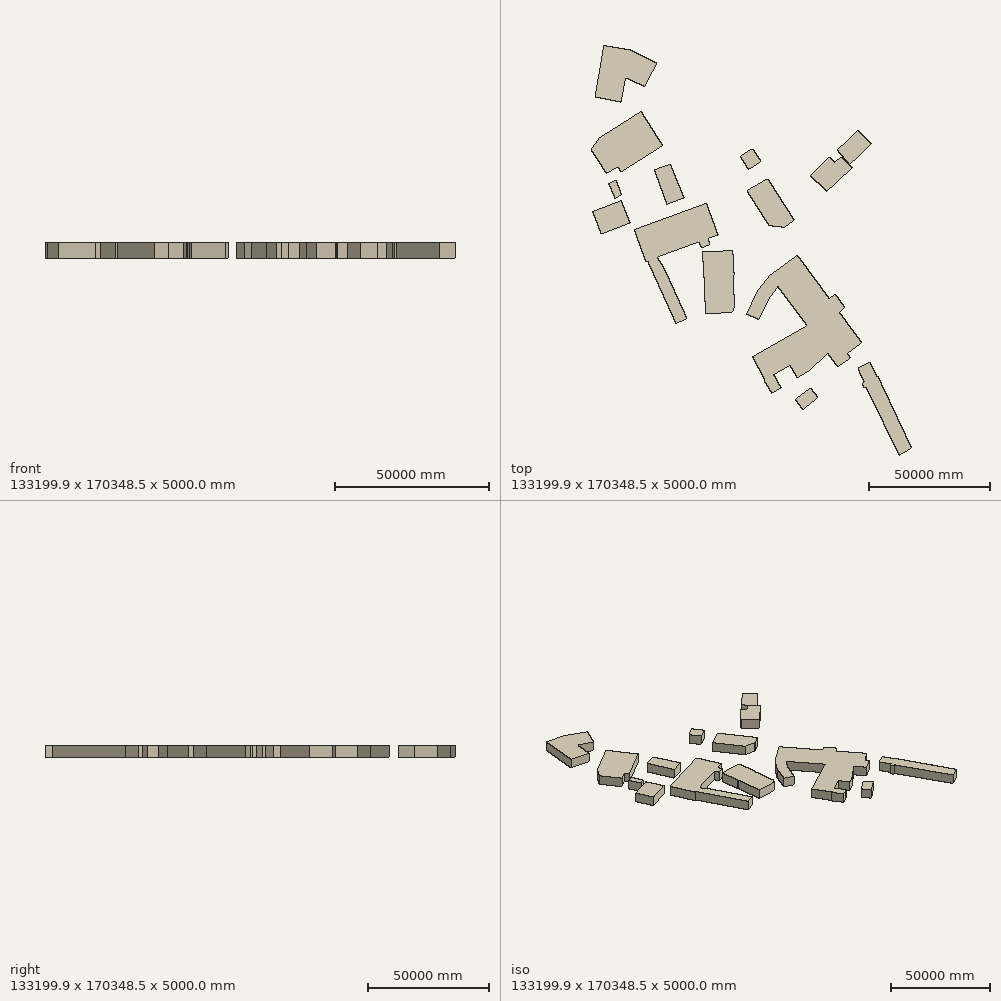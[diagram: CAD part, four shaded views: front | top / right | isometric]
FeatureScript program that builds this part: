
annotation { "Feature Type Name" : "Feature", "Feature Type Description" : "" }
export const myFeature = defineFeature(function(context is Context, id is Id, definition is map)
    precondition{}
    {
        {
            var Q0;
            Q0=qCreatedBy(makeId("Top.planeOp"),FACE);
            var sketch = newSketch(context, id + "F0", { "sketchPlane" : qUnion([Q0])});
            skLineSegment(sketch, "E0", {"start": v(9180.3, 14744.96) * mm, "end": v(-20829.56, 3751.13) * mm});
            skLineSegment(sketch, "E1", {"start": v(-20829.56, 3751.13) * mm, "end": v(-16013.77, -9394.52) * mm});
            skLineSegment(sketch, "E2", {"start": v(-16013.77, -9394.52) * mm, "end": v(13996.08, 1599.31) * mm});
            skLineSegment(sketch, "E3", {"start": v(13996.08, 1599.31) * mm, "end": v(9180.3, 14744.96) * mm});
            skLineSegment(sketch, "E4", {"start": v(-5833.22, 31019.04) * mm, "end": v(-12464.48, 28589.74) * mm});
            skLineSegment(sketch, "E5", {"start": v(-12464.48, 28589.74) * mm, "end": v(-7236.84, 14319.86) * mm});
            skLineSegment(sketch, "E6", {"start": v(-7236.84, 14319.86) * mm, "end": v(-97.14, 16935.42) * mm});
            skLineSegment(sketch, "E7", {"start": v(-97.14, 16935.42) * mm, "end": v(-5833.22, 31019.04) * mm});
            skLineSegment(sketch, "E8", {"start": v(7534.29, -5269.84) * mm, "end": v(20121.82, -4941.47) * mm});
            skLineSegment(sketch, "E9", {"start": v(20121.82, -4941.47) * mm, "end": v(20705.59, -15376.35) * mm});
            skLineSegment(sketch, "E10", {"start": v(20705.59, -15376.35) * mm, "end": v(8060.17, -16083.79) * mm});
            skLineSegment(sketch, "E11", {"start": v(8060.17, -16083.79) * mm, "end": v(7534.29, -5269.84) * mm});
            skLineSegment(sketch, "E12", {"start": v(20339.95, -15396.8) * mm, "end": v(20814.21, -28670.67) * mm});
            skLineSegment(sketch, "E13", {"start": v(20814.21, -28670.67) * mm, "end": v(19884.44, -30712.12) * mm});
            skLineSegment(sketch, "E14", {"start": v(19884.44, -30712.12) * mm, "end": v(8747.38, -30934.46) * mm});
            skLineSegment(sketch, "E15", {"start": v(8747.38, -30934.46) * mm, "end": v(8217.4, -16074.99) * mm});
            skLineSegment(sketch, "E16", {"start": v(8217.4, -16074.99) * mm, "end": v(20339.95, -15396.8) * mm});
            skLineSegment(sketch, "E17", {"start": v(1118.1, -33175.2) * mm, "end": v(-3429.25, -35227.5) * mm});
            skLineSegment(sketch, "E18", {"start": v(-3429.25, -35227.5) * mm, "end": v(-15292.92, -9130.44) * mm});
            skLineSegment(sketch, "E19", {"start": v(-15292.92, -9130.44) * mm, "end": v(-11265.11, -7654.9) * mm});
            skLineSegment(sketch, "E20", {"start": v(-11265.11, -7654.9) * mm, "end": v(-8211.31, -12609.05) * mm});
            skLineSegment(sketch, "E21", {"start": v(-8211.31, -12609.05) * mm, "end": v(1118.1, -33175.2) * mm});
            skLineSegment(sketch, "E22", {"start": v(-26224, 27727.1) * mm, "end": v(-8953.75, 38651.94) * mm});
            skLineSegment(sketch, "E23", {"start": v(-8953.75, 38651.94) * mm, "end": v(-17928.87, 52840) * mm});
            skLineSegment(sketch, "E24", {"start": v(-17928.87, 52840) * mm, "end": v(-35299.15, 41851.89) * mm});
            skLineSegment(sketch, "E25", {"start": v(-35299.15, 41851.89) * mm, "end": v(-26224, 27727.1) * mm});
            skLineSegment(sketch, "E26", {"start": v(-20806.48, 52061.88) * mm, "end": v(-3429.25, 62527.37) * mm});
            skLineSegment(sketch, "E27", {"start": v(-3429.25, 62527.37) * mm, "end": v(8188.27, 57867.5) * mm});
            skLineSegment(sketch, "E28", {"start": v(8188.27, 57867.5) * mm, "end": v(34965.39, -2872.82) * mm});
            skLineSegment(sketch, "E29", {"start": v(34965.39, -2872.82) * mm, "end": v(30408.87, -7931.69) * mm});
            skLineSegment(sketch, "E30", {"start": v(30408.87, -7931.69) * mm, "end": v(26319.23, -13071.99) * mm});
            skLineSegment(sketch, "E31", {"start": v(26319.23, -13071.99) * mm, "end": v(23024.7, -19009.4) * mm});
            skLineSegment(sketch, "E32", {"start": v(23024.7, -19009.4) * mm, "end": v(21761.11, -21238.12) * mm});
            skLineSegment(sketch, "E33", {"start": v(21761.11, -21238.12) * mm, "end": v(21988.82, -27611.3) * mm});
            skLineSegment(sketch, "E34", {"start": v(21988.82, -27611.3) * mm, "end": v(19699.51, -31756.28) * mm});
            skLineSegment(sketch, "E35", {"start": v(19699.51, -31756.28) * mm, "end": v(8762.32, -36540.5) * mm});
            skLineSegment(sketch, "E36", {"start": v(8762.32, -36540.5) * mm, "end": v(-1824.5, -41017.7) * mm});
            skLineSegment(sketch, "E37", {"start": v(-1824.5, -41017.7) * mm, "end": v(-4239.99, -35704.24) * mm});
            skLineSegment(sketch, "E38", {"start": v(-4239.99, -35704.24) * mm, "end": v(-3429.25, -35227.5) * mm});
            skLineSegment(sketch, "E39", {"start": v(-21984.25, 4257.34) * mm, "end": v(-22053.34, 5492.49) * mm});
            skLineSegment(sketch, "E40", {"start": v(-22053.34, 5492.49) * mm, "end": v(-21116.37, 5809) * mm});
            skLineSegment(sketch, "E41", {"start": v(-21116.37, 5809) * mm, "end": v(-24193.4, 13146.52) * mm});
            skLineSegment(sketch, "E42", {"start": v(-24193.4, 13146.52) * mm, "end": v(-28928.83, 26072.85) * mm});
            skLineSegment(sketch, "E43", {"start": v(-28928.83, 26072.85) * mm, "end": v(-26224, 27727.1) * mm});
            skLineSegment(sketch, "E44", {"start": v(-20806.48, 52061.88) * mm, "end": v(-20939.9, 51541.93) * mm});
            skLineSegment(sketch, "E45", {"start": v(-20939.9, 51541.93) * mm, "end": v(-35716.67, 42504.66) * mm});
            skLineSegment(sketch, "E46", {"start": v(-35716.67, 42504.66) * mm, "end": v(-35299.15, 41851.89) * mm});
            skLineSegment(sketch, "E47", {"start": v(28364.05, 37487.13) * mm, "end": v(23234.36, 34191.31) * mm});
            skPoint(sketch, "E47.startSnap0", {"position": v(28364.05, -10501.84) * mm});
            skLineSegment(sketch, "E48", {"start": v(23234.36, 34191.31) * mm, "end": v(26757.4, 28707.97) * mm});
            skLineSegment(sketch, "E49", {"start": v(26757.4, 28707.97) * mm, "end": v(31940.06, 32037.82) * mm});
            skLineSegment(sketch, "E50", {"start": v(31940.06, 32037.82) * mm, "end": v(28364.05, 37487.13) * mm});
            skLineSegment(sketch, "E51", {"start": v(-16373.54, 63248) * mm, "end": v(-26224, 56783.82) * mm});
            skLineSegment(sketch, "E52", {"start": v(-26224, 56783.82) * mm, "end": v(-37109.45, 58951.37) * mm});
            skLineSegment(sketch, "E53", {"start": v(-37109.45, 58951.37) * mm, "end": v(-33419.95, 80341.1) * mm});
            skLineSegment(sketch, "E54", {"start": v(-33419.95, 80341.1) * mm, "end": v(-22394.3, 78439.3) * mm});
            skLineSegment(sketch, "E55", {"start": v(-22394.3, 78439.3) * mm, "end": v(-11376.38, 72962.11) * mm});
            skLineSegment(sketch, "E56", {"start": v(-11376.38, 72962.11) * mm, "end": v(-16373.54, 63248) * mm});
            skLineSegment(sketch, "E57", {"start": v(-22394.3, 78439.3) * mm, "end": v(-26224, 56783.82) * mm});
            skLineSegment(sketch, "E58", {"start": v(-16373.54, 63248) * mm, "end": v(-24431.78, 66918.08) * mm});
            skLineSegment(sketch, "E59", {"start": v(6060.36, -1307.87) * mm, "end": v(7106.65, -3841.01) * mm});
            skLineSegment(sketch, "E60", {"start": v(7106.65, -3841.01) * mm, "end": v(10639.53, -2381.78) * mm});
            skLineSegment(sketch, "E61", {"start": v(10639.53, -2381.78) * mm, "end": v(9922.1, 106.85) * mm});
            skLineSegment(sketch, "E62", {"start": v(9922.1, 106.85) * mm, "end": v(6060.36, -1307.87) * mm});
            skLineSegment(sketch, "E63", {"start": v(34627.65, 24979.67) * mm, "end": v(26021.2, 19930.56) * mm});
            skLineSegment(sketch, "E64", {"start": v(26021.2, 19930.56) * mm, "end": v(35201.41, 5529.1) * mm});
            skLineSegment(sketch, "E65", {"start": v(35201.41, 5529.1) * mm, "end": v(40996.42, 4840.59) * mm});
            skLineSegment(sketch, "E66", {"start": v(40996.42, 4840.59) * mm, "end": v(41742.31, 4840.59) * mm});
            skLineSegment(sketch, "E67", {"start": v(41742.31, 4840.59) * mm, "end": v(45758.66, 7594.65) * mm});
            skLineSegment(sketch, "E68", {"start": v(45758.66, 7594.65) * mm, "end": v(34627.65, 24979.67) * mm});
            skLineSegment(sketch, "E69", {"start": v(30149.7, 22352.6) * mm, "end": v(41742.31, 4840.59) * mm});
            skLineSegment(sketch, "E70", {"start": v(30578.29, 7773.03) * mm, "end": v(35201.41, 5529.1) * mm});
            skLineSegment(sketch, "E71", {"start": v(35201.41, 5529.1) * mm, "end": v(40054.71, 218.93) * mm});
            skLineSegment(sketch, "E72", {"start": v(40054.71, 218.93) * mm, "end": v(54441.46, 15144.84) * mm});
            skLineSegment(sketch, "E73", {"start": v(54441.46, 15144.84) * mm, "end": v(24983.9, 50784.74) * mm});
            skLineSegment(sketch, "E74", {"start": v(24983.9, 50784.74) * mm, "end": v(29466.42, 54584.5) * mm});
            skLineSegment(sketch, "E75", {"start": v(29466.42, 54584.5) * mm, "end": v(50331.25, 52778.67) * mm});
            skLineSegment(sketch, "E76", {"start": v(50331.25, 52778.67) * mm, "end": v(69795.87, 29398.24) * mm});
            skLineSegment(sketch, "E77", {"start": v(69795.87, 29398.24) * mm, "end": v(54441.46, 15144.84) * mm});
            skLineSegment(sketch, "E78", {"start": v(69795.87, 29398.24) * mm, "end": v(87382.07, 45471.38) * mm});
            skLineSegment(sketch, "E79", {"start": v(87382.07, 45471.38) * mm, "end": v(86102.16, 48374.68) * mm});
            skLineSegment(sketch, "E80", {"start": v(86102.16, 48374.68) * mm, "end": v(50331.25, 52778.67) * mm});
            skLineSegment(sketch, "E81", {"start": v(-26254.73, 15803.16) * mm, "end": v(-38088.46, 11240.76) * mm});
            skLineSegment(sketch, "E82", {"start": v(-38088.46, 11240.76) * mm, "end": v(-34497.29, 1926.16) * mm});
            skLineSegment(sketch, "E83", {"start": v(-34497.29, 1926.16) * mm, "end": v(-22549.16, 6532.67) * mm});
            skLineSegment(sketch, "E84", {"start": v(-22549.16, 6532.67) * mm, "end": v(-26254.73, 15803.16) * mm});
            skLineSegment(sketch, "E85", {"start": v(-26041.33, 18190.84) * mm, "end": v(-28779.25, 16768.14) * mm});
            skLineSegment(sketch, "E86", {"start": v(-28779.25, 16768.14) * mm, "end": v(-31401.56, 22970.47) * mm});
            skLineSegment(sketch, "E87", {"start": v(-31401.56, 22970.47) * mm, "end": v(-28276.36, 24291.79) * mm});
            skLineSegment(sketch, "E88", {"start": v(-28276.36, 24291.79) * mm, "end": v(-26041.33, 18190.84) * mm});
            skLineSegment(sketch, "E89", {"start": v(-22053.34, 5492.49) * mm, "end": v(-38449.89, -829.07) * mm});
            skLineSegment(sketch, "E90", {"start": v(-38449.89, -829.07) * mm, "end": v(-42275.12, 8741.87) * mm});
            skLineSegment(sketch, "E91", {"start": v(-42275.12, 8741.87) * mm, "end": v(-39703.87, 35545.65) * mm});
            skLineSegment(sketch, "E92", {"start": v(-39703.87, 35545.65) * mm, "end": v(-35299.15, 41851.89) * mm});
            skLineSegment(sketch, "E93", {"start": v(-38708.22, 36971.12) * mm, "end": v(-33806.78, 39529.13) * mm});
            skLineSegment(sketch, "E94", {"start": v(-33806.78, 39529.13) * mm, "end": v(-27624.16, 29906.34) * mm});
            skLineSegment(sketch, "E95", {"start": v(-27624.16, 29906.34) * mm, "end": v(-32273.96, 27072.47) * mm});
            skLineSegment(sketch, "E96", {"start": v(-32273.96, 27072.47) * mm, "end": v(-38708.22, 36971.12) * mm});
            skLineSegment(sketch, "E97", {"start": v(67362.54, 27139.4) * mm, "end": v(60192.45, 34090.6) * mm});
            skLineSegment(sketch, "E98", {"start": v(60192.45, 34090.6) * mm, "end": v(52497.57, 26153.42) * mm});
            skLineSegment(sketch, "E99", {"start": v(52497.57, 26153.42) * mm, "end": v(59249.23, 19607.86) * mm});
            skLineSegment(sketch, "E100", {"start": v(59249.23, 19607.86) * mm, "end": v(67362.54, 27139.4) * mm});
            skLineSegment(sketch, "E101", {"start": v(62601.55, 31755.05) * mm, "end": v(65198.22, 33916.82) * mm});
            skLineSegment(sketch, "E102", {"start": v(65198.22, 33916.82) * mm, "end": v(69795.87, 29398.24) * mm});
            skLineSegment(sketch, "E103", {"start": v(63603.34, 36836.56) * mm, "end": v(72237.77, 44924.05) * mm});
            skLineSegment(sketch, "E104", {"start": v(72237.77, 44924.05) * mm, "end": v(77928.18, 39457.99) * mm});
            skLineSegment(sketch, "E105", {"start": v(77928.18, 39457.99) * mm, "end": v(68720.24, 30690.25) * mm});
            skLineSegment(sketch, "E106", {"start": v(68720.24, 30690.25) * mm, "end": v(63603.34, 36836.56) * mm});
            skLineSegment(sketch, "E107", {"start": v(20622.92, -45797.36) * mm, "end": v(25984.33, -31295.17) * mm});
            skLineSegment(sketch, "E108", {"start": v(25984.33, -31295.17) * mm, "end": v(30115.26, -22154.4) * mm});
            skLineSegment(sketch, "E109", {"start": v(30115.26, -22154.4) * mm, "end": v(35564.57, -15298.81) * mm});
            skLineSegment(sketch, "E110", {"start": v(35564.57, -15298.81) * mm, "end": v(45320.59, -6597.5) * mm});
            skLineSegment(sketch, "E111", {"start": v(45320.59, -6597.5) * mm, "end": v(54109.8, -1499.75) * mm});
            skLineSegment(sketch, "E112", {"start": v(54109.8, -1499.75) * mm, "end": v(59176.91, -2659.02) * mm});
            skLineSegment(sketch, "E113", {"start": v(59176.91, -2659.02) * mm, "end": v(96270.22, -26197.03) * mm});
            skLineSegment(sketch, "E114", {"start": v(96270.22, -26197.03) * mm, "end": v(87423.55, -61215.11) * mm});
            skLineSegment(sketch, "E115", {"start": v(87423.55, -61215.11) * mm, "end": v(96940.67, -88958.78) * mm});
            skLineSegment(sketch, "E116", {"start": v(96940.67, -88958.78) * mm, "end": v(81552.41, -102683.44) * mm});
            skLineSegment(sketch, "E117", {"start": v(81552.41, -102683.44) * mm, "end": v(64179.6, -94307.53) * mm});
            skLineSegment(sketch, "E118", {"start": v(64179.6, -94307.53) * mm, "end": v(44495.13, -73160.65) * mm});
            skLineSegment(sketch, "E119", {"start": v(44495.13, -73160.65) * mm, "end": v(32253.96, -60281.3) * mm});
            skLineSegment(sketch, "E120", {"start": v(32253.96, -60281.3) * mm, "end": v(20622.92, -45797.36) * mm});
            skLineSegment(sketch, "E121", {"start": v(25984.33, -31295.17) * mm, "end": v(30988.59, -33556.7) * mm});
            skLineSegment(sketch, "E122", {"start": v(30988.59, -33556.7) * mm, "end": v(35448.3, -24670.2) * mm});
            skLineSegment(sketch, "E123", {"start": v(35448.3, -24670.2) * mm, "end": v(30115.26, -22154.4) * mm});
            skLineSegment(sketch, "E124", {"start": v(35448.3, -24670.2) * mm, "end": v(38935.45, -19937.73) * mm});
            skLineSegment(sketch, "E125", {"start": v(38935.45, -19937.73) * mm, "end": v(35564.57, -15298.81) * mm});
            skLineSegment(sketch, "E126", {"start": v(38935.45, -19937.73) * mm, "end": v(63760.5, -53220.33) * mm});
            skLineSegment(sketch, "E127", {"start": v(63760.5, -53220.33) * mm, "end": v(69124.55, -49553.86) * mm});
            skLineSegment(sketch, "E128", {"start": v(69124.55, -49553.86) * mm, "end": v(67846.96, -47684.75) * mm});
            skLineSegment(sketch, "E129", {"start": v(67846.96, -47684.75) * mm, "end": v(73836.1, -43233.3) * mm});
            skLineSegment(sketch, "E130", {"start": v(73836.1, -43233.3) * mm, "end": v(70802.6, -39151.92) * mm});
            skLineSegment(sketch, "E131", {"start": v(70802.6, -39151.92) * mm, "end": v(59535.48, -47555.91) * mm});
            skLineSegment(sketch, "E132", {"start": v(70802.6, -39151.92) * mm, "end": v(64478.1, -30672.76) * mm});
            skLineSegment(sketch, "E133", {"start": v(64478.1, -30672.76) * mm, "end": v(66749.96, -28566.09) * mm});
            skLineSegment(sketch, "E134", {"start": v(66749.96, -28566.09) * mm, "end": v(62798.25, -23081.93) * mm});
            skLineSegment(sketch, "E135", {"start": v(62798.25, -23081.93) * mm, "end": v(60281.34, -24895.54) * mm});
            skLineSegment(sketch, "E136", {"start": v(60281.34, -24895.54) * mm, "end": v(47004.15, -6901.18) * mm});
            skLineSegment(sketch, "E137", {"start": v(47004.15, -6901.18) * mm, "end": v(35564.57, -15298.81) * mm});
            skLineSegment(sketch, "E138", {"start": v(41969.4, -64552.95) * mm, "end": v(39595.86, -65929.6) * mm});
            skLineSegment(sketch, "E139", {"start": v(39595.86, -65929.6) * mm, "end": v(38044.2, -63254.32) * mm});
            skLineSegment(sketch, "E140", {"start": v(38044.2, -63254.32) * mm, "end": v(40513.77, -61821.97) * mm});
            skLineSegment(sketch, "E141", {"start": v(40513.77, -61821.97) * mm, "end": v(42004.46, -64552.95) * mm});
            skLineSegment(sketch, "E142", {"start": v(38044.2, -63254.32) * mm, "end": v(36373.97, -64061.52) * mm});
            skLineSegment(sketch, "E143", {"start": v(36373.97, -64061.52) * mm, "end": v(32969.1, -58733.53) * mm});
            skLineSegment(sketch, "E144", {"start": v(32969.1, -58733.53) * mm, "end": v(37193.65, -56526.67) * mm});
            skLineSegment(sketch, "E145", {"start": v(37193.65, -56526.67) * mm, "end": v(40228.95, -61987.16) * mm});
            skLineSegment(sketch, "E146", {"start": v(33421.6, -58497.15) * mm, "end": v(28325.27, -49109.24) * mm});
            skLineSegment(sketch, "E147", {"start": v(28325.27, -49109.24) * mm, "end": v(51011.07, -36127.34) * mm});
            skLineSegment(sketch, "E148", {"start": v(46456.64, -38733.6) * mm, "end": v(51795.05, -48062.45) * mm});
            skLineSegment(sketch, "E149", {"start": v(51795.05, -48062.45) * mm, "end": v(37193.65, -56526.67) * mm});
            skLineSegment(sketch, "E150", {"start": v(38338.13, -43379.4) * mm, "end": v(47019.68, -57797.32) * mm});
            skLineSegment(sketch, "E151", {"start": v(47019.68, -57797.32) * mm, "end": v(52455.15, -54524.43) * mm});
            skLineSegment(sketch, "E152", {"start": v(52455.15, -54524.43) * mm, "end": v(49155.07, -49592.8) * mm});
            skLineSegment(sketch, "E153", {"start": v(52455.15, -54524.43) * mm, "end": v(55697.23, -51211.68) * mm});
            skLineSegment(sketch, "E154", {"start": v(55697.23, -51211.68) * mm, "end": v(56110.25, -51211.68) * mm});
            skLineSegment(sketch, "E155", {"start": v(56110.25, -51211.68) * mm, "end": v(59535.48, -47555.91) * mm});
            skLineSegment(sketch, "E156", {"start": v(46113.69, -66798.09) * mm, "end": v(52455.15, -62016.4) * mm});
            skLineSegment(sketch, "E157", {"start": v(52455.15, -62016.4) * mm, "end": v(55625.93, -66005.4) * mm});
            skLineSegment(sketch, "E158", {"start": v(55625.93, -66005.4) * mm, "end": v(49329.85, -71010.03) * mm});
            skLineSegment(sketch, "E159", {"start": v(49329.85, -71010.03) * mm, "end": v(46113.69, -66798.09) * mm});
            skLineSegment(sketch, "E160", {"start": v(72037.68, -53810.51) * mm, "end": v(77127.07, -51328.5) * mm});
            skLineSegment(sketch, "E161", {"start": v(77127.07, -51328.5) * mm, "end": v(79985.15, -57220.15) * mm});
            skLineSegment(sketch, "E162", {"start": v(79985.15, -57220.15) * mm, "end": v(73901.35, -60171.44) * mm});
            skLineSegment(sketch, "E163", {"start": v(73901.35, -60171.44) * mm, "end": v(74666.05, -61945.13) * mm});
            skLineSegment(sketch, "E164", {"start": v(74666.05, -61945.13) * mm, "end": v(75482.36, -61612.56) * mm});
            skLineSegment(sketch, "E165", {"start": v(75482.36, -61612.56) * mm, "end": v(89319.3, -90007.35) * mm});
            skLineSegment(sketch, "E166", {"start": v(89319.3, -90007.35) * mm, "end": v(94491.68, -87047.48) * mm});
            skLineSegment(sketch, "E167", {"start": v(94491.68, -87047.48) * mm, "end": v(80324.52, -56953.23) * mm});
            skLineSegment(sketch, "E168", {"start": v(80324.52, -56953.23) * mm, "end": v(79985.15, -57220.15) * mm});
            skLineSegment(sketch, "E169", {"start": v(81861.25, -74702.67) * mm, "end": v(87408.1, -72091.44) * mm});
            skPoint(sketch, "E169.endSnap0", {"position": v(87408.1, -72000.35) * mm});
            skLineSegment(sketch, "E170", {"start": v(72037.68, -53810.51) * mm, "end": v(74890.6, -59691.54) * mm});
            skLineSegment(sketch, "E171", {"start": v(-7263.1, 7302.62) * mm, "end": v(-3163.08, -3889.23) * mm});
            skSolve(sketch);
        }
        {
            var Q0;
            Q0=makeQuery(id+"F0.imprint","IMPRINT",FACE,{"disambiguationData":[TD([[makeQuery(id+"F0.imprint","IMPRINT",EDGE,{"derivedFrom":sQuery(id+"F0.wireOp",EDGE,"E4")}),1.0]])]});
            var Q1;
            Q1=makeQuery(id+"F0.imprint","IMPRINT",FACE,{"disambiguationData":[TD([[makeQuery(id+"F0.imprint","IMPRINT",EDGE,{"derivedFrom":sQuery(id+"F0.wireOp",EDGE,"E47")}),1.0]])]});
            var Q2;
            Q2=makeQuery(id+"F0.imprint","IMPRINT",FACE,{"disambiguationData":[TD([[makeQuery(id+"F0.imprint","IMPRINT",EDGE,{"derivedFrom":sQuery(id+"F0.wireOp",EDGE,"E8")}),-1.0]])]});
            var Q3;
            Q3=makeQuery(id+"F0.imprint","IMPRINT",FACE,{"disambiguationData":[TD([[makeQuery(id+"F0.imprint","IMPRINT",EDGE,{"derivedFrom":sQuery(id+"F0.wireOp",EDGE,"E12")}),-1.0]])]});
            var Q4;
            Q4=makeQuery(id+"F0.imprint","IMPRINT",FACE,{"disambiguationData":[TD([[makeQuery(id+"F0.imprint","IMPRINT",EDGE,{"derivedFrom":sQuery(id+"F0.wireOp",EDGE,"E17")}),-1.0]])]});
            var Q5;
            Q5=makeQuery(id+"F0.imprint","IMPRINT",FACE,{"disambiguationData":[TD([[makeQuery(id+"F0.imprint","IMPRINT",EDGE,{"derivedFrom":sQuery(id+"F0.wireOp",EDGE,"E59")}),1.0]])]});
            var Q6;
            Q6=makeQuery(id+"F0.imprint","IMPRINT",FACE,{"disambiguationData":[TD([[makeQuery(id+"F0.imprint","IMPRINT",EDGE,{"derivedFrom":sQuery(id+"F0.wireOp",EDGE,"E67")}),1.0]])]});
            var Q7;
            {var subQ0=sQuery(id+"F0.wireOp",EDGE,"E64");Q7=makeQuery(id+"F0.imprint","IMPRINT",FACE,{"disambiguationData":[TD([[makeQuery(id+"F0.imprint","IMPRINT",EDGE,{"derivedFrom":subQ0}),1.0]])]});}
            var Q8;
            Q8=makeQuery(id+"F0.imprint","IMPRINT",FACE,{"disambiguationData":[TD([[makeQuery(id+"F0.imprint","IMPRINT",EDGE,{"derivedFrom":sQuery(id+"F0.wireOp",EDGE,"E85")}),-1.0]])]});
            var Q9;
            Q9=makeQuery(id+"F0.imprint","IMPRINT",FACE,{"disambiguationData":[TD([[makeQuery(id+"F0.imprint","IMPRINT",EDGE,{"derivedFrom":sQuery(id+"F0.wireOp",EDGE,"E0")}),1.0]])]});
            var Q10;
            {var subQ3=sQuery(id+"F0.wireOp",EDGE,"E93");Q10=makeQuery(id+"F0.imprint","IMPRINT",FACE,{"disambiguationData":[TD([[makeQuery(id+"F0.imprint","IMPRINT",EDGE,{"derivedFrom":subQ3}),1.0]])]});}
            var Q11;
            {var subQ3=sQuery(id+"F0.wireOp",EDGE,"E52");Q11=makeQuery(id+"F0.imprint","IMPRINT",FACE,{"disambiguationData":[TD([[makeQuery(id+"F0.imprint","IMPRINT",EDGE,{"derivedFrom":subQ3}),-1.0]])]});}
            var Q12;
            {var subQ0=sQuery(id+"F0.wireOp",EDGE,"E55");Q12=makeQuery(id+"F0.imprint","IMPRINT",FACE,{"disambiguationData":[TD([[makeQuery(id+"F0.imprint","IMPRINT",EDGE,{"derivedFrom":subQ0}),-1.0]])]});}
            var Q13;
            {var subQ3=sQuery(id+"F0.wireOp",EDGE,"E22");Q13=makeQuery(id+"F0.imprint","IMPRINT",FACE,{"disambiguationData":[TD([[makeQuery(id+"F0.imprint","IMPRINT",EDGE,{"derivedFrom":subQ3}),1.0]])]});}
            var Q14;
            Q14=makeQuery(id+"F0.imprint","IMPRINT",FACE,{"disambiguationData":[TD([[makeQuery(id+"F0.imprint","IMPRINT",EDGE,{"derivedFrom":sQuery(id+"F0.wireOp",EDGE,"E93")}),-1.0]])]});
            var Q15;
            Q15=makeQuery(id+"F0.imprint","IMPRINT",FACE,{"disambiguationData":[TD([[makeQuery(id+"F0.imprint","IMPRINT",EDGE,{"derivedFrom":sQuery(id+"F0.wireOp",EDGE,"E81")}),1.0]])]});
            var Q16;
            {var subQ0=sQuery(id+"F0.wireOp",EDGE,"E98");Q16=makeQuery(id+"F0.imprint","IMPRINT",FACE,{"disambiguationData":[TD([[makeQuery(id+"F0.imprint","IMPRINT",EDGE,{"derivedFrom":subQ0}),1.0]])]});}
            var Q17;
            {var subQ4=sQuery(id+"F0.wireOp",EDGE,"E101");Q17=makeQuery(id+"F0.imprint","IMPRINT",FACE,{"disambiguationData":[TD([[makeQuery(id+"F0.imprint","IMPRINT",EDGE,{"derivedFrom":subQ4}),-1.0]])]});}
            var Q18;
            Q18=makeQuery(id+"F0.imprint","IMPRINT",FACE,{"disambiguationData":[TD([[makeQuery(id+"F0.imprint","IMPRINT",EDGE,{"derivedFrom":sQuery(id+"F0.wireOp",EDGE,"E103")}),-1.0]])]});
            var Q19;
            {var subQ3=sQuery(id+"F0.wireOp",EDGE,"E125");Q19=makeQuery(id+"F0.imprint","IMPRINT",FACE,{"disambiguationData":[TD([[makeQuery(id+"F0.imprint","IMPRINT",EDGE,{"derivedFrom":subQ3}),-1.0]])]});}
            var Q20;
            {var subQ1=sQuery(id+"F0.wireOp",EDGE,"E148");Q20=makeQuery(id+"F0.imprint","IMPRINT",FACE,{"disambiguationData":[TD([[makeQuery(id+"F0.imprint","IMPRINT",EDGE,{"derivedFrom":subQ1}),1.0]])]});}
            var Q21;
            {var subQ4=sQuery(id+"F0.wireOp",EDGE,"E148");Q21=makeQuery(id+"F0.imprint","IMPRINT",FACE,{"disambiguationData":[TD([[makeQuery(id+"F0.imprint","IMPRINT",EDGE,{"derivedFrom":subQ4}),-1.0]])]});}
            var Q22;
            {var subQ6=sQuery(id+"F0.wireOp",EDGE,"E146");Q22=makeQuery(id+"F0.imprint","IMPRINT",FACE,{"disambiguationData":[TD([[makeQuery(id+"F0.imprint","IMPRINT",EDGE,{"derivedFrom":subQ6}),-1.0]])]});}
            var Q23;
            {var subQ3=sQuery(id+"F0.wireOp",EDGE,"E142");Q23=makeQuery(id+"F0.imprint","IMPRINT",FACE,{"disambiguationData":[TD([[makeQuery(id+"F0.imprint","IMPRINT",EDGE,{"derivedFrom":subQ3}),-1.0]])]});}
            var Q24;
            {var subQ4=sQuery(id+"F0.wireOp",EDGE,"E151");Q24=makeQuery(id+"F0.imprint","IMPRINT",FACE,{"disambiguationData":[TD([[makeQuery(id+"F0.imprint","IMPRINT",EDGE,{"derivedFrom":subQ4}),1.0]])]});}
            var Q25;
            Q25=makeQuery(id+"F0.imprint","IMPRINT",FACE,{"disambiguationData":[TD([[makeQuery(id+"F0.imprint","IMPRINT",EDGE,{"derivedFrom":sQuery(id+"F0.wireOp",EDGE,"E156")}),-1.0]])]});
            var Q26;
            Q26=makeQuery(id+"F0.imprint","IMPRINT",FACE,{"disambiguationData":[TD([[makeQuery(id+"F0.imprint","IMPRINT",EDGE,{"derivedFrom":sQuery(id+"F0.wireOp",EDGE,"E108")}),-1.0]])]});
            var Q27;
            Q27=makeQuery(id+"F0.imprint","IMPRINT",FACE,{"disambiguationData":[TD([[makeQuery(id+"F0.imprint","IMPRINT",EDGE,{"derivedFrom":sQuery(id+"F0.wireOp",EDGE,"E109")}),-1.0]])]});
            var Q28;
            Q28=makeQuery(id+"F0.imprint","IMPRINT",FACE,{"disambiguationData":[TD([[makeQuery(id+"F0.imprint","IMPRINT",EDGE,{"derivedFrom":sQuery(id+"F0.wireOp",EDGE,"E160")}),-1.0]])]});
            var Q29;
            {var subQ1=sQuery(id+"F0.wireOp",EDGE,"E163");Q29=makeQuery(id+"F0.imprint","IMPRINT",FACE,{"disambiguationData":[TD([[makeQuery(id+"F0.imprint","IMPRINT",EDGE,{"derivedFrom":subQ1}),1.0]])]});}
            var Q30;
            {var subQ0=sQuery(id+"F0.wireOp",EDGE,"E127");Q30=makeQuery(id+"F0.imprint","IMPRINT",FACE,{"disambiguationData":[TD([[makeQuery(id+"F0.imprint","IMPRINT",EDGE,{"derivedFrom":subQ0}),1.0]])]});}
            extrude(context, id + "F1", {"entities" : qUnion([Q0, Q1, Q2, Q3, Q4, Q5, Q6, Q7, Q8, Q9, Q10, Q11, Q12, Q13, Q14, Q15, Q16, Q17, Q18, Q19, Q20, Q21, Q22, Q23, Q24, Q25, Q26, Q27, Q28, Q29, Q30]), "depth" : 5000 * mm, "offsetDistance" : 25 * mm});
        }
    });
